# Revit family: Aquas Pool Package APN0285
name_source: partatom
category: Mechanical Equipment
revit_build: Autodesk Revit 2016 (Build: 20151007_0715(x64)
units: mm (PartAtom-declared; Revit-internal decimal feet)

## family parameters
Always vertical = Yes
Cut with Voids When Loaded = No
OmniClass Number = 23.65.35.11.17
OmniClass Title = Thermodynamic Water Heaters
Part Type = Normal
Room Calculation Point = No
Round Connector Dimension = Use Diameter
Shared = No
Work Plane-Based = No

## types (1)
- APN285
    # of Electrical Connections = 1
    AIR INLET SIZE = 3"
    A_HEIGHT = 46 1/2"
    Air Inlet Height = 37"
    Air Inlet Offset = 11 3/4"
    B_UNIT WIDTH = 15 3/4"
    Boiler Depth = 17"
    C_UNIT DEPTH = 34"
    Condensate Diameter = 1/2"
    D_Pool Hex Width = 28 1/2"
    E_Pool Conn Height = 6 3/4"
    FUEL TYPE = NATURAL GAS
    Fuel Type = Natural Gas or LP
    GALLON CAPACITY = 4.9
    GAS CONN SIZE = 1/2"
    Gas Conn Height = 31"
    Gas Conn Offset = 4 1/4"
    Heat Exchanger Diameter = 3 1/2"
    Heat Exchanger Flange Diameter = 5"
    INPUT RATE (BTUH) = 285,000
    MODEL NO. = APN285
    Manufacturer = Lochinvar
    Model = APN285
    OUTPUT RATE (BTUH) = 270,750
    POOL INLET CONN SIZE = 2 1/2"
    POOL OUTLET CONN SIZE = 2 1/2"
    Pool Conn Diameter = 2 1/2"
    SES BIM Studio # = 18 0649 06
    Total Amps = <12
    URL = http://www.lochinvar.com
    VENT SIZE = 3"
    Vent Conn Height = 16 3/4"
    Voltage/Control = 24
    Voltage/Heater = 120

## geometry (parser evidence)
native form markers: Sweep x2
no freeform markers — native parametric forms only
